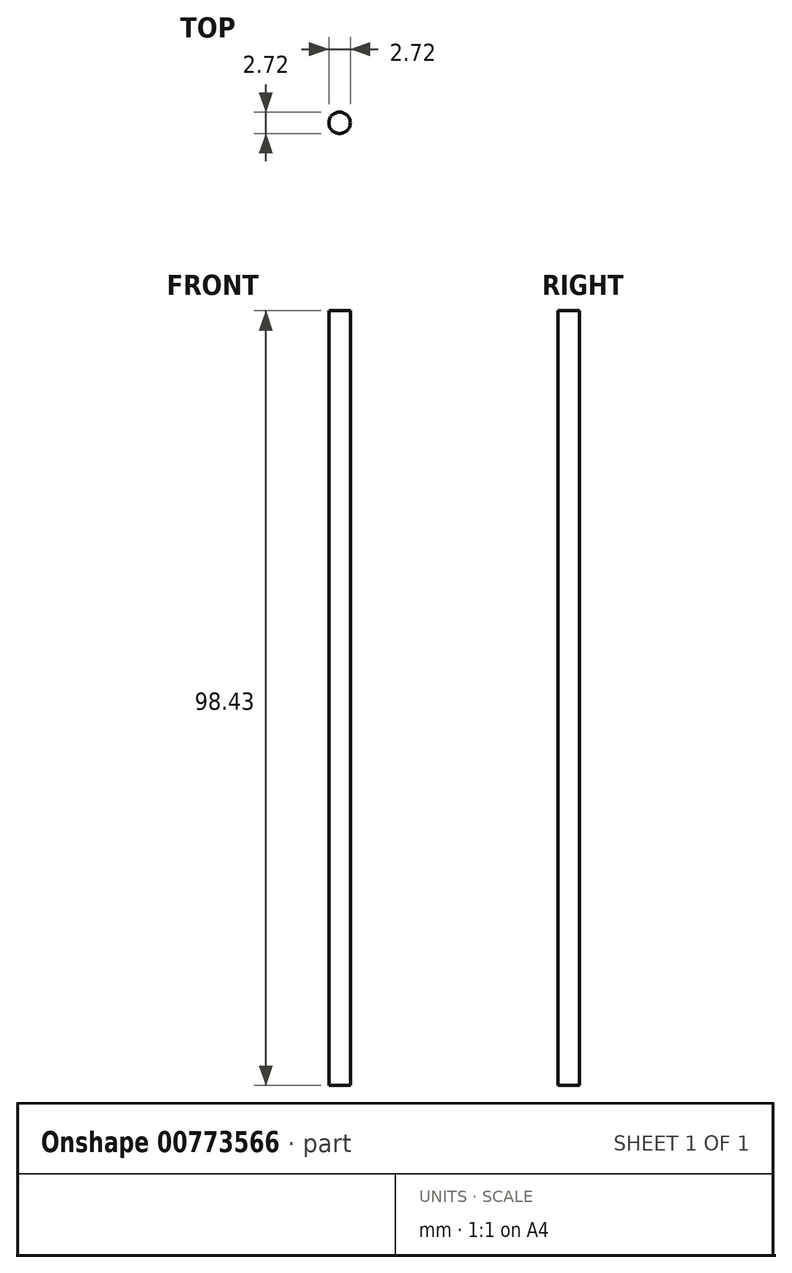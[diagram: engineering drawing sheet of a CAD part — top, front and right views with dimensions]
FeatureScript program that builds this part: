
annotation { "Feature Type Name" : "Feature", "Feature Type Description" : "" }
export const myFeature = defineFeature(function(context is Context, id is Id, definition is map)
    precondition{}
    {
        {
            var Q0;
            Q0=qCreatedBy(makeId("Front.planeOp"),FACE);
            var sketch = newSketch(context, id + "F0", { "sketchPlane" : qUnion([Q0])});
            skLineSegment(sketch, "E0.bottom", {"start": v(0, 0) * mm, "end": v(1.36, 0) * mm});
            skLineSegment(sketch, "E0.top", {"start": v(0, 98.43) * mm, "end": v(1.36, 98.43) * mm});
            skLineSegment(sketch, "E0.left", {"start": v(0, 0) * mm, "end": v(0, 98.43) * mm});
            skLineSegment(sketch, "E0.right", {"start": v(1.36, 0) * mm, "end": v(1.36, 98.43) * mm});
            skSolve(sketch);
        }
        {
            var Q0;
            Q0=makeQuery(id+"F0.imprint","IMPRINT",FACE,{"disambiguationData":[TD([[makeQuery(id+"F0.imprint","IMPRINT",EDGE,{"derivedFrom":sQuery(id+"F0.wireOp",EDGE,"E0.bottom")}),1.0]])]});
            var Q1;
            Q1=sQuery(id+"F0.wireOp",EDGE,"E0.left");
            revolve(context, id + "F1", {"surfaceOperationType" : NewSurfaceOperationType.NEW, "entities" : qUnion([Q0]), "axis" : qUnion([Q1]), "revolveType" : RevolveType.FULL});
        }
    });
